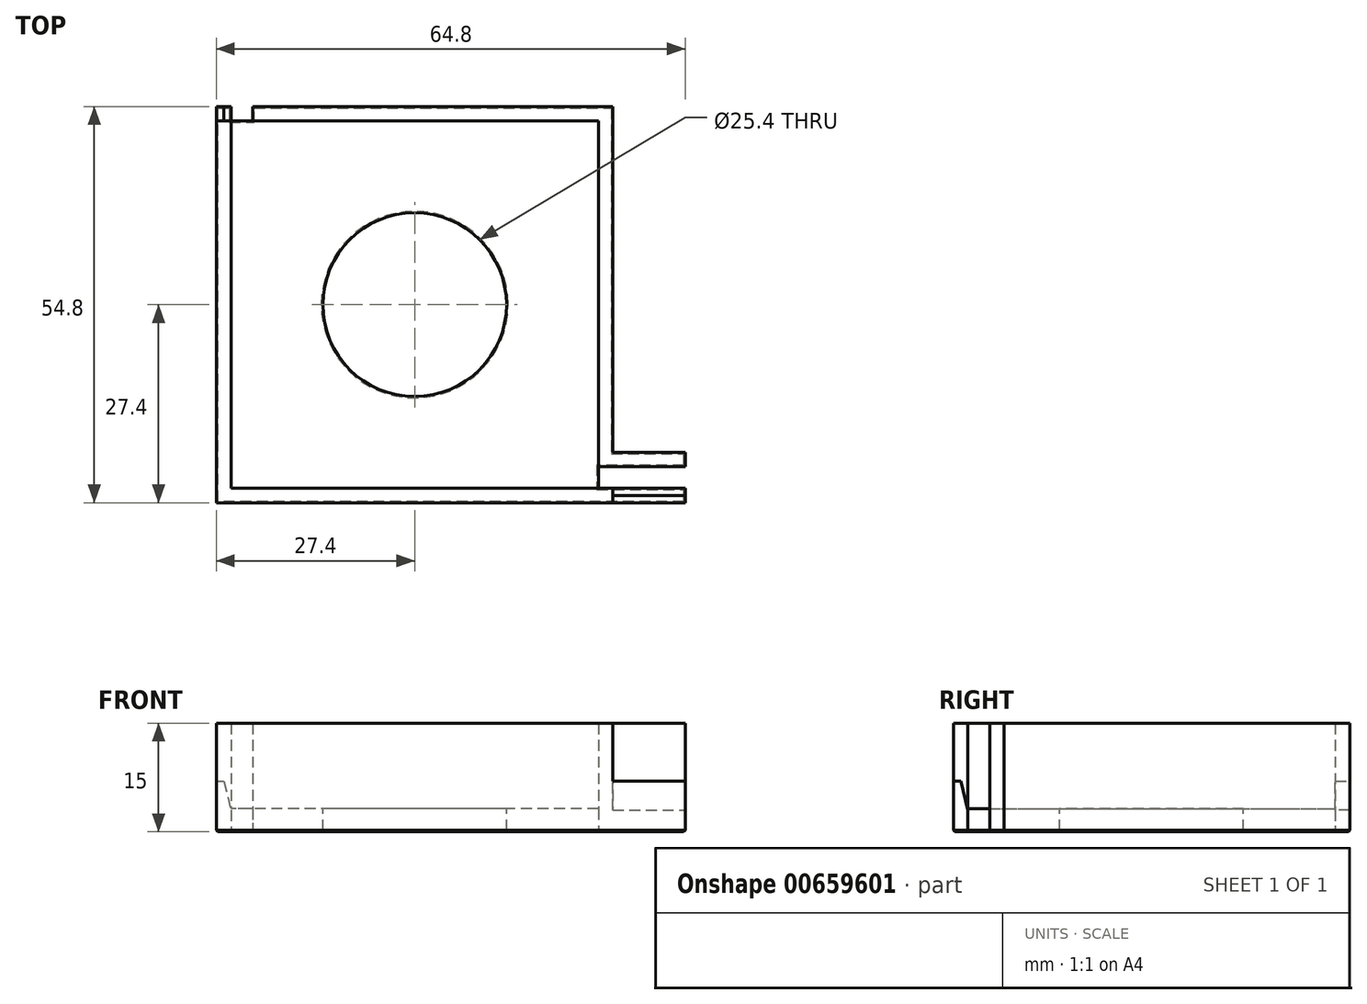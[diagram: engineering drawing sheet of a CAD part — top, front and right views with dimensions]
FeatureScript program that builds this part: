
annotation { "Feature Type Name" : "Feature", "Feature Type Description" : "" }
export const myFeature = defineFeature(function(context is Context, id is Id, definition is map)
    precondition{}
    {
        {
            var Q0;
            Q0=qCreatedBy(makeId("Top.planeOp"),FACE);
            var sketch = newSketch(context, id + "F0", { "sketchPlane" : qUnion([Q0])});
            skLineSegment(sketch, "E0.bottom", {"start": v(25.4, -25.4) * mm, "end": v(-25.4, -25.4) * mm});
            skLineSegment(sketch, "E0.top", {"start": v(25.4, 25.4) * mm, "end": v(-25.4, 25.4) * mm});
            skLineSegment(sketch, "E0.left", {"start": v(25.4, -25.4) * mm, "end": v(25.4, 25.4) * mm});
            skLineSegment(sketch, "E0.right", {"start": v(-25.4, -25.4) * mm, "end": v(-25.4, 25.4) * mm});
            skPoint(sketch, "E0.middle", {"position": v(0, 0) * mm});
            skLineSegment(sketch, "E1.0", {"start": v(27.4, -27.4) * mm, "end": v(27.4, 27.4) * mm});
            skLineSegment(sketch, "E1.1", {"start": v(27.4, -27.4) * mm, "end": v(-27.4, -27.4) * mm});
            skLineSegment(sketch, "E1.2", {"start": v(-27.4, -27.4) * mm, "end": v(-27.4, 27.4) * mm});
            skLineSegment(sketch, "E1.3", {"start": v(27.4, 27.4) * mm, "end": v(-27.4, 27.4) * mm});
            skLineSegment(sketch, "E2", {"start": v(25.4, -22.4) * mm, "end": v(27.4, -22.4) * mm});
            skLineSegment(sketch, "E3", {"start": v(25.4, -25.4) * mm, "end": v(27.4, -25.4) * mm});
            skLineSegment(sketch, "E4", {"start": v(-25.4, 25.4) * mm, "end": v(-25.4, 27.4) * mm});
            skLineSegment(sketch, "E5", {"start": v(-25.4, 27.4) * mm, "end": v(-22.4, 27.4) * mm});
            skLineSegment(sketch, "E6", {"start": v(-22.4, 27.4) * mm, "end": v(-22.4, 25.4) * mm});
            skLineSegment(sketch, "E7.bottom", {"start": v(27.4, -25.4) * mm, "end": v(37.4, -25.4) * mm});
            skLineSegment(sketch, "E7.top", {"start": v(27.4, -27.4) * mm, "end": v(37.4, -27.4) * mm});
            skLineSegment(sketch, "E7.left", {"start": v(27.4, -25.4) * mm, "end": v(27.4, -27.4) * mm});
            skLineSegment(sketch, "E7.right", {"start": v(37.4, -25.4) * mm, "end": v(37.4, -27.4) * mm});
            skLineSegment(sketch, "E8.bottom", {"start": v(27.4, -22.4) * mm, "end": v(37.4, -22.4) * mm});
            skLineSegment(sketch, "E8.top", {"start": v(27.4, -20.4) * mm, "end": v(37.4, -20.4) * mm});
            skLineSegment(sketch, "E8.left", {"start": v(27.4, -22.4) * mm, "end": v(27.4, -20.4) * mm});
            skLineSegment(sketch, "E8.right", {"start": v(37.4, -22.4) * mm, "end": v(37.4, -20.4) * mm});
            skLineSegment(sketch, "E9.bottom", {"start": v(-25.4, 27.4) * mm, "end": v(-27.4, 27.4) * mm});
            skLineSegment(sketch, "E9.top", {"start": v(-25.4, 35.4) * mm, "end": v(-27.4, 35.4) * mm});
            skLineSegment(sketch, "E9.left", {"start": v(-25.4, 27.4) * mm, "end": v(-25.4, 35.4) * mm});
            skLineSegment(sketch, "E9.right", {"start": v(-27.4, 27.4) * mm, "end": v(-27.4, 35.4) * mm});
            skLineSegment(sketch, "E10.bottom", {"start": v(-22.4, 27.4) * mm, "end": v(-20.4, 27.4) * mm});
            skLineSegment(sketch, "E10.top", {"start": v(-22.4, 35.4) * mm, "end": v(-20.4, 35.4) * mm});
            skLineSegment(sketch, "E10.left", {"start": v(-22.4, 27.4) * mm, "end": v(-22.4, 35.4) * mm});
            skLineSegment(sketch, "E10.right", {"start": v(-20.4, 27.4) * mm, "end": v(-20.4, 35.4) * mm});
            skSolve(sketch);
        }
        {
            var Q0;
            Q0=makeQuery(id+"F0.imprint","IMPRINT",FACE,{"disambiguationData":[TD([[makeQuery(id+"F0.imprint","IMPRINT",EDGE,{"derivedFrom":sQuery(id+"F0.wireOp",EDGE,"E0.bottom")}),-1.0]])]});
            extrude(context, id + "F1", {"entities" : qUnion([Q0]), "depth" : 3.17 * mm, "offsetDistance" : 25 * mm});
        }
        {
            var Q0;
            Q0=makeQuery(id+"F0.imprint","IMPRINT",FACE,{"disambiguationData":[TD([[makeQuery(id+"F0.imprint","IMPRINT",EDGE,{"derivedFrom":sQuery(id+"F0.wireOp",EDGE,"E0.bottom")}),1.0]])]});
            var Q1;
            {var subQ3=sQuery(id+"F0.wireOp",EDGE,"E2");Q1=makeQuery(id+"F0.imprint","IMPRINT",FACE,{"disambiguationData":[TD([[makeQuery(id+"F0.imprint","IMPRINT",EDGE,{"derivedFrom":subQ3}),1.0]])]});}
            var Q2;
            Q2=makeQuery(id+"F0.imprint","IMPRINT",FACE,{"disambiguationData":[TD([[makeQuery(id+"F0.imprint","IMPRINT",EDGE,{"derivedFrom":sQuery(id+"F0.wireOp",EDGE,"E10.bottom")}),1.0]])]});
            var Q3;
            Q3=makeQuery(id+"F0.imprint","IMPRINT",FACE,{"disambiguationData":[TD([[makeQuery(id+"F0.imprint","IMPRINT",EDGE,{"derivedFrom":sQuery(id+"F0.wireOp",EDGE,"E9.bottom")}),-1.0]])]});
            var Q4;
            Q4=makeQuery(id+"F0.imprint","IMPRINT",FACE,{"disambiguationData":[TD([[makeQuery(id+"F0.imprint","IMPRINT",EDGE,{"derivedFrom":sQuery(id+"F0.wireOp",EDGE,"E7.bottom")}),-1.0]])]});
            var Q5;
            Q5=makeQuery(id+"F0.imprint","IMPRINT",FACE,{"disambiguationData":[TD([[makeQuery(id+"F0.imprint","IMPRINT",EDGE,{"derivedFrom":sQuery(id+"F0.wireOp",EDGE,"E8.bottom")}),1.0]])]});
            extrude(context, id + "F2", {"entities" : qUnion([Q0, Q1, Q2, Q3, Q4, Q5]), "operationType" : NewBodyOperationType.ADD, "depth" : 7 * mm, "offsetDistance" : 25 * mm});
        }
        {
            var Q0;
            Q0=makeQuery(id+"F2.opExtrude","CAP_FACE",FACE,{"disambiguationData":[OSD([sQuery(id+"F0.wireOp",EDGE,"E0.bottom"),sQuery(id+"F0.wireOp",EDGE,"E0.right"),sQuery(id+"F0.wireOp",EDGE,"E1.1"),sQuery(id+"F0.wireOp",EDGE,"E1.2"),sQuery(id+"F0.wireOp",EDGE,"E3"),sQuery(id+"F0.wireOp",EDGE,"E4"),sQuery(id+"F0.wireOp",EDGE,"E7.bottom"),sQuery(id+"F0.wireOp",EDGE,"E7.top"),sQuery(id+"F0.wireOp",EDGE,"E7.right"),sQuery(id+"F0.wireOp",EDGE,"E9.top"),sQuery(id+"F0.wireOp",EDGE,"E9.left"),sQuery(id+"F0.wireOp",EDGE,"E9.right")])],"isStart":false});
            var sketch = newSketch(context, id + "F3", { "sketchPlane" : qUnion([Q0])});
            skLineSegment(sketch, "E11.bottom", {"start": v(37.4, -25.4) * mm, "end": v(27.4, -25.4) * mm});
            skLineSegment(sketch, "E11.top", {"start": v(37.4, -27.4) * mm, "end": v(27.4, -27.4) * mm});
            skLineSegment(sketch, "E11.left", {"start": v(37.4, -25.4) * mm, "end": v(37.4, -27.4) * mm});
            skLineSegment(sketch, "E11.right", {"start": v(27.4, -25.4) * mm, "end": v(27.4, -27.4) * mm});
            skLineSegment(sketch, "E12.bottom", {"start": v(-27.4, 35.4) * mm, "end": v(-25.4, 35.4) * mm});
            skLineSegment(sketch, "E12.top", {"start": v(-27.4, 25.4) * mm, "end": v(-25.4, 25.4) * mm});
            skLineSegment(sketch, "E12.left", {"start": v(-27.4, 35.4) * mm, "end": v(-27.4, 25.4) * mm});
            skLineSegment(sketch, "E12.right", {"start": v(-25.4, 35.4) * mm, "end": v(-25.4, 25.4) * mm});
            skSolve(sketch);
        }
        {
            var Q0;
            {var subQ4=sQuery(id+"F3.wireOp",EDGE,"E11.right");Q0=makeQuery(id+"F3.imprint","IMPRINT",FACE,{"disambiguationData":[TD([[makeQuery(id+"F3.imprint","IMPRINT",EDGE,{"derivedFrom":subQ4}),-1.0]])]});}
            var Q1;
            Q1=makeQuery(id+"F2.opExtrude","CAP_FACE",FACE,{"disambiguationData":[OSD([sQuery(id+"F0.wireOp",EDGE,"E0.top"),sQuery(id+"F0.wireOp",EDGE,"E0.left"),sQuery(id+"F0.wireOp",EDGE,"E1.0"),sQuery(id+"F0.wireOp",EDGE,"E1.3"),sQuery(id+"F0.wireOp",EDGE,"E2"),sQuery(id+"F0.wireOp",EDGE,"E6"),sQuery(id+"F0.wireOp",EDGE,"E8.bottom"),sQuery(id+"F0.wireOp",EDGE,"E8.top"),sQuery(id+"F0.wireOp",EDGE,"E8.right"),sQuery(id+"F0.wireOp",EDGE,"E10.top"),sQuery(id+"F0.wireOp",EDGE,"E10.left"),sQuery(id+"F0.wireOp",EDGE,"E10.right")])],"isStart":false});
            extrude(context, id + "F4", {"entities" : qUnion([Q0, Q1]), "operationType" : NewBodyOperationType.ADD, "depth" : 8 * mm, "offsetDistance" : 25 * mm});
        }
        {
            var Q0;
            Q0=makeQuery(id+"F1.opExtrude","CAP_FACE",FACE,{"disambiguationData":[OSD([sQuery(id+"F0.wireOp",EDGE,"E0.bottom"),sQuery(id+"F0.wireOp",EDGE,"E0.top"),sQuery(id+"F0.wireOp",EDGE,"E0.left"),sQuery(id+"F0.wireOp",EDGE,"E0.right")])],"isStart":false});
            var sketch = newSketch(context, id + "F5", { "sketchPlane" : qUnion([Q0])});
            skCircle(sketch, "E13", {"center": v(0, 0) * mm, "radius": 12.7 * mm});
            skSolve(sketch);
        }
        {
            var Q0;
            Q0=makeQuery(id+"F5.imprint","IMPRINT",FACE,{"disambiguationData":[TD([[makeQuery(id+"F5.imprint","IMPRINT",EDGE,{"derivedFrom":sQuery(id+"F5.wireOp",EDGE,"E13")}),1.0]])]});
            extrude(context, id + "F6", {"entities" : qUnion([Q0]), "operationType" : NewBodyOperationType.REMOVE, "oppositeDirection" : true, "depth" : 25.4 * mm, "offsetDistance" : 25.4 * mm});
        }
        {
            var Q0;
            Q0=makeQuery(id+"F2.opExtrude","CAP_EDGE",EDGE,{"disambiguationData":[OSD([sQuery(id+"F0.wireOp",EDGE,"E0.bottom"),sQuery(id+"F0.wireOp",EDGE,"E3"),sQuery(id+"F0.wireOp",EDGE,"E7.bottom")])],"isStart":false});
            chamfer(context, id + "F7", {"entities" : qUnion([Q0]), "chamferType" : ChamferType.TWO_OFFSETS, "width1" : 4 * mm, "oppositeDirection" : false, "width2" : 1 * mm, "tangentPropagation" : true});
        }
        {
            var Q0;
            Q0=makeQuery(id+"F2.opExtrude","CAP_EDGE",EDGE,{"disambiguationData":[OSD([sQuery(id+"F0.wireOp",EDGE,"E0.right"),sQuery(id+"F0.wireOp",EDGE,"E4"),sQuery(id+"F0.wireOp",EDGE,"E9.left")])],"isStart":false});
            chamfer(context, id + "F8", {"entities" : qUnion([Q0]), "chamferType" : ChamferType.TWO_OFFSETS, "width1" : 1 * mm, "oppositeDirection" : false, "width2" : 4 * mm, "tangentPropagation" : true});
        }
        {
            var Q0;
            {var subQ0=sQuery(id+"F0.wireOp",EDGE,"E0.left");var subQ1=sQuery(id+"F0.wireOp",EDGE,"E0.top");var subQ2=sQuery(id+"F0.wireOp",EDGE,"E0.right");var subQ3=sQuery(id+"F0.wireOp",EDGE,"E0.bottom");Q0=makeQuery(id+"F2.boolean.opBoolean","MERGE",FACE,{"derivedFrom":[makeQuery(id+"F1.opExtrude","CAP_FACE",FACE,{"disambiguationData":[OSD([subQ3,subQ1,subQ0,subQ2])],"isStart":true}),makeQuery(id+"F2.opExtrude","CAP_FACE",FACE,{"disambiguationData":[OSD([subQ3,subQ2,sQuery(id+"F0.wireOp",EDGE,"E1.1"),sQuery(id+"F0.wireOp",EDGE,"E1.2"),sQuery(id+"F0.wireOp",EDGE,"E3"),sQuery(id+"F0.wireOp",EDGE,"E4"),sQuery(id+"F0.wireOp",EDGE,"E7.bottom"),sQuery(id+"F0.wireOp",EDGE,"E7.top"),sQuery(id+"F0.wireOp",EDGE,"E7.right"),sQuery(id+"F0.wireOp",EDGE,"E9.top"),sQuery(id+"F0.wireOp",EDGE,"E9.left"),sQuery(id+"F0.wireOp",EDGE,"E9.right")])],"isStart":true}),makeQuery(id+"F2.opExtrude","CAP_FACE",FACE,{"disambiguationData":[OSD([subQ1,subQ0,sQuery(id+"F0.wireOp",EDGE,"E1.0"),sQuery(id+"F0.wireOp",EDGE,"E1.3"),sQuery(id+"F0.wireOp",EDGE,"E2"),sQuery(id+"F0.wireOp",EDGE,"E6"),sQuery(id+"F0.wireOp",EDGE,"E8.bottom"),sQuery(id+"F0.wireOp",EDGE,"E8.top"),sQuery(id+"F0.wireOp",EDGE,"E8.right"),sQuery(id+"F0.wireOp",EDGE,"E10.top"),sQuery(id+"F0.wireOp",EDGE,"E10.left"),sQuery(id+"F0.wireOp",EDGE,"E10.right")])],"isStart":true})]});}
            chamfer(context, id + "F9", {"entities" : qUnion([Q0]), "width" : .2 * mm, "tangentPropagation" : true});
        }
    });
